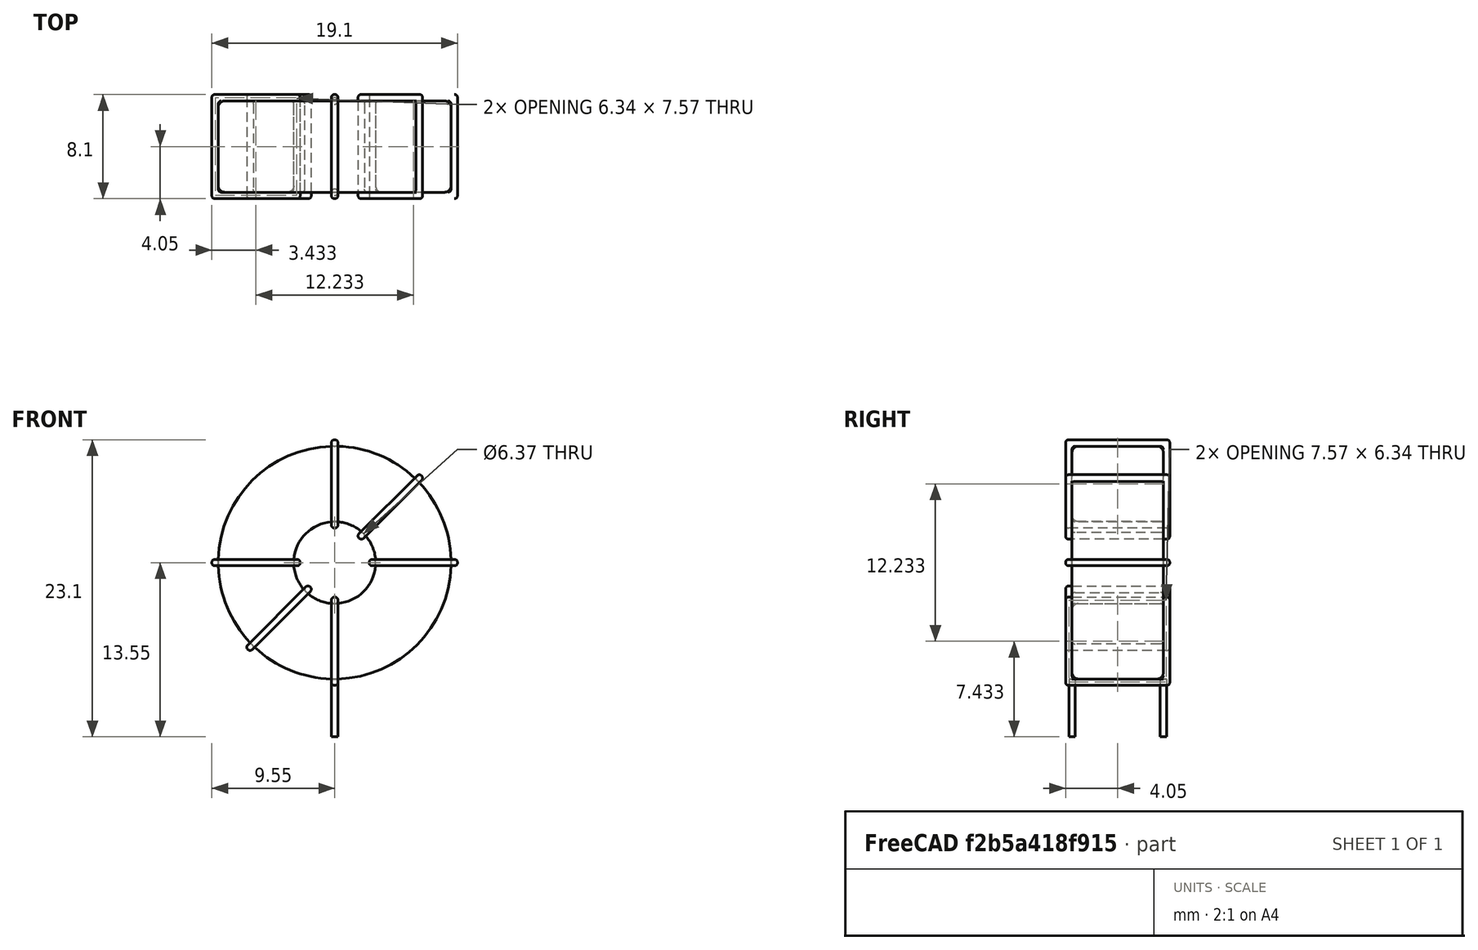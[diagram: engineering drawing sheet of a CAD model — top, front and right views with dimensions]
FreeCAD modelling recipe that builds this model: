
FCSTD DOCUMENT  (FreeCAD 0.16R6703 (Git))
Label: L_Toroid_Vertical_L19.1mm_W8.1mm_P7.10mm_Bourns_5700series
License: All rights reserved
LicenseURL: http://en.wikipedia.org/wiki/All_rights_reserved
objects: Sketcher::SketchObject×6, PartDesign::Pad×6, PartDesign::Fillet×5, Spreadsheet::Sheet×1
note: 23 computed .brp shape members not serialized (recipe doc carries the construction recipe); baked Part::Feature solids carry a one-line shape summary decoded from their .brp

FEATURE [Spreadsheet::Sheet] Spreadsheet  label="dimensions"
  cells = A1=Wx; B1(Wx)=19.1; C1(WW)=6.366666666666667; D1=19.1; A2=Wy; B2(Wy)=8.1; D2=8.1; A3=RM; B3(RMx)=7.1; C3(RMy)=0; A4=d_wire; B4(d_wire)=0.5; A5=H; B5(H)=19.1; A6=offsetx; B6(offsetx)=9.550000000000001
FEATURE [Sketcher::SketchObject] Sketch
  Placement = pos=(0,-3.55,0) rot=(1,0,0;1.5708rad)
  expr: Placement.Base.y = -Spreadsheet.RMx / 2
  expr: Constraints[0] = Spreadsheet.Wx / 2 - Spreadsheet.d_wire
  expr: Constraints[4] = Spreadsheet.WW / 2
  expr: Constraints[2] = Spreadsheet.Wx / 2 + Spreadsheet.d_wire + 0.5
  sketch-geometry (2):
    g0: Circle CenterX=0 CenterY=10.55 CenterZ=0 NormalX=0 NormalY=0 NormalZ=1 Radius=9.05
    g1: Circle CenterX=0 CenterY=10.55 CenterZ=0 NormalX=0 NormalY=0 NormalZ=1 Radius=3.18333
  constraints (5):
    c: Radius(g0) = 9.05
    c: DistanceX(g-1,g0) = 0
    c: DistanceY(g-1,g0) = 10.55
    c: Coincident(g1,g0)
    c: Radius(g1) = 3.18333
FEATURE [PartDesign::Pad] Pad
  Length = 7.1
  Length2 = 100
  Midplane = true
  Placement = pos=(0,-3.55,0) rot=(1,0,0;1.5708rad)
  Sketch = -> Sketch
  Type = 0
  expr: Length = Spreadsheet.Wy - 2 * Spreadsheet.d_wire
FEATURE [Sketcher::SketchObject] Sketch001
  Placement = pos=(0,0,1) rot=(0,0,1;0rad)
  expr: Placement.Base.z = 0.5 + Spreadsheet.d_wire
  expr: Constraints[4] = Spreadsheet.RMy
  expr: Constraints[2] = -Spreadsheet.RMx
  expr: Constraints[1] = Spreadsheet.d_wire / 2
  sketch-geometry (2):
    g0: Circle CenterX=0 CenterY=0 CenterZ=0 NormalX=0 NormalY=0 NormalZ=1 Radius=0.25
    g1: Circle CenterX=0 CenterY=-7.1 CenterZ=0 NormalX=0 NormalY=0 NormalZ=1 Radius=0.25
  constraints (5):
    c: Equal(g0,g1)
    c: Radius(g0) = 0.25
    c: DistanceY(g-1,g1) = -7.1
    c: Coincident(g0,g-1)
    c: DistanceX(g-1,g1) = 0
FEATURE [PartDesign::Pad] Pad001
  Length = 0.5
  Length2 = 4
  Placement = pos=(0,0,1) rot=(0,0,1;0rad)
  Reversed = true
  Sketch = -> Sketch001
  Type = 4
  expr: Length2 = 3.5 + Spreadsheet.d_wire
  expr: Length = Spreadsheet.d_wire
FEATURE [PartDesign::Fillet] Fillet
  Base = -> Pad [Edge6,Edge3,Edge2]
  Placement = pos=(0,-3.55,0) rot=(1,0,0;1.5708rad)
  Radius = 0.5
FEATURE [Sketcher::SketchObject] Sketch003
  Placement = pos=(0,0.5,10.55) rot=(1,0,0;3.14159rad)
  expr: Constraints[18] = Spreadsheet.d_wire
  expr: Constraints[16] = Spreadsheet.d_wire
  expr: Constraints[19] = Spreadsheet.d_wire
  expr: Constraints[17] = Spreadsheet.d_wire
  expr: Placement.Base.y = -1 * (Spreadsheet.RMx - Spreadsheet.Wy) / 2
  expr: Constraints[21] = (Spreadsheet.Wx - Spreadsheet.WW) / 2 - Spreadsheet.d_wire
  expr: Constraints[22] = Spreadsheet.Wx / 2 - Spreadsheet.d_wire
  expr: Constraints[43] = Spreadsheet.d_wire
  expr: Constraints[48] = Spreadsheet.Wx - Spreadsheet.d_wire * 2
  expr: Constraints[49] = Spreadsheet.Wy
  expr: Placement.Base.z = Spreadsheet.Wx / 2 + Spreadsheet.d_wire + 0.5
  sketch-geometry (16):
    g0: LineSegment StartX=-2.68333 StartY=0 StartZ=0 EndX=-9.55 EndY=0 EndZ=0
    g1: LineSegment StartX=-9.55 StartY=0 StartZ=0 EndX=-9.55 EndY=8.1 EndZ=0
    g2: LineSegment StartX=-9.55 StartY=8.1 StartZ=0 EndX=-2.68333 EndY=8.1 EndZ=0
    g3: LineSegment StartX=-2.68333 StartY=8.1 StartZ=0 EndX=-2.68333 EndY=0 EndZ=0
    g4: LineSegment StartX=-9.05 StartY=7.6 StartZ=0 EndX=-3.18333 EndY=7.6 EndZ=0
    g5: LineSegment StartX=-3.18333 StartY=7.6 StartZ=0 EndX=-3.18333 EndY=0.5 EndZ=0
    g6: LineSegment StartX=-3.18333 StartY=0.5 StartZ=0 EndX=-9.05 EndY=0.5 EndZ=0
    g7: LineSegment StartX=-9.05 StartY=0.5 StartZ=0 EndX=-9.05 EndY=7.6 EndZ=0
    g8: LineSegment StartX=2.68333 StartY=8.1 StartZ=0 EndX=9.55 EndY=8.1 EndZ=0
    g9: LineSegment StartX=9.55 StartY=8.1 StartZ=0 EndX=9.55 EndY=0 EndZ=0
    g10: LineSegment StartX=9.55 StartY=0 StartZ=0 EndX=2.68333 EndY=0 EndZ=0
    g11: LineSegment StartX=2.68333 StartY=0 StartZ=0 EndX=2.68333 EndY=8.1 EndZ=0
    g12: LineSegment StartX=3.18333 StartY=7.6 StartZ=0 EndX=9.05 EndY=7.6 EndZ=0
    g13: LineSegment StartX=9.05 StartY=7.6 StartZ=0 EndX=9.05 EndY=0.5 EndZ=0
    g14: LineSegment StartX=9.05 StartY=0.5 StartZ=0 EndX=3.18333 EndY=0.5 EndZ=0
    g15: LineSegment StartX=3.18333 StartY=0.5 StartZ=0 EndX=3.18333 EndY=7.6 EndZ=0
  constraints (50):
    c: Horizontal(g0)
    c: Coincident(g1,g0)
    c: Vertical(g1)
    c: Coincident(g2,g1)
    c: Horizontal(g2)
    c: Coincident(g3,g2)
    c: Coincident(g3,g0)
    c: Vertical(g3)
    c: Coincident(g4,g5)
    c: Coincident(g5,g6)
    c: Coincident(g6,g7)
    c: Coincident(g7,g4)
    c: Horizontal(g4)
    c: Horizontal(g6)
    c: Vertical(g5)
    c: Vertical(g7)
    c: DistanceX(g1,g4) = 0.5
    c: DistanceY(g4,g1) = 0.5
    c: DistanceX(g5,g0) = 0.5
    c: DistanceY(g0,g5) = 0.5
    c: DistanceY(g-1,g0) = 0
    c: DistanceX(g6,g6) = 5.86667
    c: DistanceX(g6,g-1) = 9.05
    c: Coincident(g8,g9)
    c: Coincident(g9,g10)
    c: Coincident(g10,g11)
    c: Coincident(g11,g8)
    c: Horizontal(g8)
    c: Horizontal(g10)
    c: Vertical(g9)
    c: Vertical(g11)
    c: Coincident(g12,g13)
    c: Coincident(g13,g14)
    c: Coincident(g14,g15)
    c: Coincident(g15,g12)
    c: Horizontal(g12)
    c: Horizontal(g14)
    c: Vertical(g13)
    c: Vertical(g15)
    c: DistanceY(g8,g2) = 0
    c: DistanceY(g10,g0) = 0
    c: DistanceY(g14,g5) = 0
    c: DistanceY(g12,g4) = 0
    c: DistanceX(g8,g12) = 0.5
    c: Equal(g8,g2)
    c: Equal(g12,g4)
    c: Equal(g9,g1)
    c: Equal(g13,g7)
    c: DistanceX(g4,g12) = 18.1
    c: DistanceY(g0,g1) = 8.1
FEATURE [PartDesign::Pad] Pad002
  Length = 0.5
  Length2 = 100
  Midplane = true
  Placement = pos=(0,0.5,10.55) rot=(1,0,0;3.14159rad)
  Sketch = -> Sketch003
  Type = 0
  expr: Length = Spreadsheet.d_wire
FEATURE [PartDesign::Fillet] Fillet001
  Base = -> Pad002 [Edge38,Edge41,Edge42,Edge43,Edge29,Edge32,Edge33,Edge34,Edge25,Edge35,Edge36,Edge13,Edge14,Edge15,Edge16,Edge17,Edge18,Edge19,Edge1,Edge2,Edge3,Edge4,Edge5,Edge6,Edge7,Edge37,Edge39,Edge40,Edge20,Edge23,Edge24,Edge21,Edge22,Edge8,Edge9,Edge10,Edge11,Edge12,Edge26,Edge27,+8 more]
  Placement = pos=(0,0.5,10.55) rot=(1,0,0;3.14159rad)
  Radius = 0.235
  expr: Radius = Spreadsheet.d_wire * 0.47
FEATURE [Sketcher::SketchObject] Sketch004
  Placement = pos=(0,0.5,10.55) rot=(0.92388,0,0.382683;3.14159rad)
  expr: Constraints[18] = Spreadsheet.d_wire
  expr: Constraints[16] = Spreadsheet.d_wire
  expr: Constraints[19] = Spreadsheet.d_wire
  expr: Constraints[17] = Spreadsheet.d_wire
  expr: Placement.Base.y = -1 * (Spreadsheet.RMx - Spreadsheet.Wy) / 2
  expr: Constraints[21] = (Spreadsheet.Wx - Spreadsheet.WW) / 2 - Spreadsheet.d_wire
  expr: Constraints[22] = Spreadsheet.Wx / 2 - Spreadsheet.d_wire
  expr: Constraints[43] = Spreadsheet.d_wire
  expr: Constraints[48] = Spreadsheet.Wx - 2 * Spreadsheet.d_wire
  expr: Constraints[49] = Spreadsheet.Wy
  expr: Placement.Base.z = Spreadsheet.Wx / 2 + Spreadsheet.d_wire + 0.5
  sketch-geometry (16):
    g0: LineSegment StartX=-2.68333 StartY=0 StartZ=0 EndX=-9.55 EndY=0 EndZ=0
    g1: LineSegment StartX=-9.55 StartY=0 StartZ=0 EndX=-9.55 EndY=8.1 EndZ=0
    g2: LineSegment StartX=-9.55 StartY=8.1 StartZ=0 EndX=-2.68333 EndY=8.1 EndZ=0
    g3: LineSegment StartX=-2.68333 StartY=8.1 StartZ=0 EndX=-2.68333 EndY=0 EndZ=0
    g4: LineSegment StartX=-9.05 StartY=7.6 StartZ=0 EndX=-3.18333 EndY=7.6 EndZ=0
    g5: LineSegment StartX=-3.18333 StartY=7.6 StartZ=0 EndX=-3.18333 EndY=0.5 EndZ=0
    g6: LineSegment StartX=-3.18333 StartY=0.5 StartZ=0 EndX=-9.05 EndY=0.5 EndZ=0
    g7: LineSegment StartX=-9.05 StartY=0.5 StartZ=0 EndX=-9.05 EndY=7.6 EndZ=0
    g8: LineSegment StartX=2.68333 StartY=8.1 StartZ=0 EndX=9.55 EndY=8.1 EndZ=0
    g9: LineSegment StartX=9.55 StartY=8.1 StartZ=0 EndX=9.55 EndY=0 EndZ=0
    g10: LineSegment StartX=9.55 StartY=0 StartZ=0 EndX=2.68333 EndY=0 EndZ=0
    g11: LineSegment StartX=2.68333 StartY=0 StartZ=0 EndX=2.68333 EndY=8.1 EndZ=0
    g12: LineSegment StartX=3.18333 StartY=7.6 StartZ=0 EndX=9.05 EndY=7.6 EndZ=0
    g13: LineSegment StartX=9.05 StartY=7.6 StartZ=0 EndX=9.05 EndY=0.5 EndZ=0
    g14: LineSegment StartX=9.05 StartY=0.5 StartZ=0 EndX=3.18333 EndY=0.5 EndZ=0
    g15: LineSegment StartX=3.18333 StartY=0.5 StartZ=0 EndX=3.18333 EndY=7.6 EndZ=0
  constraints (50):
    c: Horizontal(g0)
    c: Coincident(g1,g0)
    c: Vertical(g1)
    c: Coincident(g2,g1)
    c: Horizontal(g2)
    c: Coincident(g3,g2)
    c: Coincident(g3,g0)
    c: Vertical(g3)
    c: Coincident(g4,g5)
    c: Coincident(g5,g6)
    c: Coincident(g6,g7)
    c: Coincident(g7,g4)
    c: Horizontal(g4)
    c: Horizontal(g6)
    c: Vertical(g5)
    c: Vertical(g7)
    c: DistanceX(g1,g4) = 0.5
    c: DistanceY(g4,g1) = 0.5
    c: DistanceX(g5,g0) = 0.5
    c: DistanceY(g0,g5) = 0.5
    c: DistanceY(g-1,g0) = 0
    c: DistanceX(g6,g6) = 5.86667
    c: DistanceX(g6,g-1) = 9.05
    c: Coincident(g8,g9)
    c: Coincident(g9,g10)
    c: Coincident(g10,g11)
    c: Coincident(g11,g8)
    c: Horizontal(g8)
    c: Horizontal(g10)
    c: Vertical(g9)
    c: Vertical(g11)
    c: Coincident(g12,g13)
    c: Coincident(g13,g14)
    c: Coincident(g14,g15)
    c: Coincident(g15,g12)
    c: Horizontal(g12)
    c: Horizontal(g14)
    c: Vertical(g13)
    c: Vertical(g15)
    c: DistanceY(g8,g2) = 0
    c: DistanceY(g10,g0) = 0
    c: DistanceY(g14,g5) = 0
    c: DistanceY(g12,g4) = 0
    c: DistanceX(g8,g12) = 0.5
    c: Equal(g8,g2)
    c: Equal(g12,g4)
    c: Equal(g9,g1)
    c: Equal(g13,g7)
    c: DistanceX(g4,g12) = 18.1
    c: DistanceY(g0,g1) = 8.1
FEATURE [PartDesign::Pad] Pad003
  Length = 0.5
  Length2 = 100
  Midplane = true
  Placement = pos=(0,0.5,10.55) rot=(0.92388,0,0.382683;3.14159rad)
  Sketch = -> Sketch004
  Type = 0
  expr: Length = Spreadsheet.d_wire
FEATURE [PartDesign::Fillet] Fillet002
  Base = -> Pad003 [Edge38,Edge41,Edge42,Edge43,Edge29,Edge32,Edge33,Edge34,Edge25,Edge35,Edge36,Edge13,Edge14,Edge15,Edge16,Edge17,Edge18,Edge19,Edge1,Edge2,Edge3,Edge4,Edge5,Edge6,Edge7,Edge37,Edge39,Edge40,Edge20,Edge23,Edge24,Edge21,Edge22,Edge8,Edge9,Edge10,Edge11,Edge12,Edge26,Edge27,+8 more]
  Placement = pos=(0,0.5,10.55) rot=(0.92388,0,0.382683;3.14159rad)
  Radius = 0.235
  expr: Radius = Spreadsheet.d_wire * 0.47
FEATURE [Sketcher::SketchObject] Sketch005
  Placement = pos=(0,0.5,10.55) rot=(0.92388,0,-0.382683;3.14159rad)
  expr: Constraints[18] = Spreadsheet.d_wire
  expr: Constraints[16] = Spreadsheet.d_wire
  expr: Constraints[19] = Spreadsheet.d_wire
  expr: Constraints[17] = Spreadsheet.d_wire
  expr: Placement.Base.y = -1 * (Spreadsheet.RMx - Spreadsheet.Wy) / 2
  expr: Constraints[21] = (Spreadsheet.Wx - Spreadsheet.WW) / 2 - Spreadsheet.d_wire
  expr: Constraints[22] = Spreadsheet.Wx / 2 - Spreadsheet.d_wire
  expr: Constraints[43] = Spreadsheet.d_wire
  expr: Constraints[48] = Spreadsheet.Wx - 2 * Spreadsheet.d_wire
  expr: Constraints[49] = Spreadsheet.Wy
  expr: Placement.Base.z = Spreadsheet.Wx / 2 + Spreadsheet.d_wire + 0.5
  sketch-geometry (16):
    g0: LineSegment StartX=-2.68333 StartY=0 StartZ=0 EndX=-9.55 EndY=0 EndZ=0
    g1: LineSegment StartX=-9.55 StartY=0 StartZ=0 EndX=-9.55 EndY=8.1 EndZ=0
    g2: LineSegment StartX=-9.55 StartY=8.1 StartZ=0 EndX=-2.68333 EndY=8.1 EndZ=0
    g3: LineSegment StartX=-2.68333 StartY=8.1 StartZ=0 EndX=-2.68333 EndY=0 EndZ=0
    g4: LineSegment StartX=-9.05 StartY=7.6 StartZ=0 EndX=-3.18333 EndY=7.6 EndZ=0
    g5: LineSegment StartX=-3.18333 StartY=7.6 StartZ=0 EndX=-3.18333 EndY=0.5 EndZ=0
    g6: LineSegment StartX=-3.18333 StartY=0.5 StartZ=0 EndX=-9.05 EndY=0.5 EndZ=0
    g7: LineSegment StartX=-9.05 StartY=0.5 StartZ=0 EndX=-9.05 EndY=7.6 EndZ=0
    g8: LineSegment StartX=2.68333 StartY=8.1 StartZ=0 EndX=9.55 EndY=8.1 EndZ=0
    g9: LineSegment StartX=9.55 StartY=8.1 StartZ=0 EndX=9.55 EndY=0 EndZ=0
    g10: LineSegment StartX=9.55 StartY=0 StartZ=0 EndX=2.68333 EndY=0 EndZ=0
    g11: LineSegment StartX=2.68333 StartY=0 StartZ=0 EndX=2.68333 EndY=8.1 EndZ=0
    g12: LineSegment StartX=3.18333 StartY=7.6 StartZ=0 EndX=9.05 EndY=7.6 EndZ=0
    g13: LineSegment StartX=9.05 StartY=7.6 StartZ=0 EndX=9.05 EndY=0.5 EndZ=0
    g14: LineSegment StartX=9.05 StartY=0.5 StartZ=0 EndX=3.18333 EndY=0.5 EndZ=0
    g15: LineSegment StartX=3.18333 StartY=0.5 StartZ=0 EndX=3.18333 EndY=7.6 EndZ=0
  constraints (50):
    c: Horizontal(g0)
    c: Coincident(g1,g0)
    c: Vertical(g1)
    c: Coincident(g2,g1)
    c: Horizontal(g2)
    c: Coincident(g3,g2)
    c: Coincident(g3,g0)
    c: Vertical(g3)
    c: Coincident(g4,g5)
    c: Coincident(g5,g6)
    c: Coincident(g6,g7)
    c: Coincident(g7,g4)
    c: Horizontal(g4)
    c: Horizontal(g6)
    c: Vertical(g5)
    c: Vertical(g7)
    c: DistanceX(g1,g4) = 0.5
    c: DistanceY(g4,g1) = 0.5
    c: DistanceX(g5,g0) = 0.5
    c: DistanceY(g0,g5) = 0.5
    c: DistanceY(g-1,g0) = 0
    c: DistanceX(g6,g6) = 5.86667
    c: DistanceX(g6,g-1) = 9.05
    c: Coincident(g8,g9)
    c: Coincident(g9,g10)
    c: Coincident(g10,g11)
    c: Coincident(g11,g8)
    c: Horizontal(g8)
    c: Horizontal(g10)
    c: Vertical(g9)
    c: Vertical(g11)
    c: Coincident(g12,g13)
    c: Coincident(g13,g14)
    c: Coincident(g14,g15)
    c: Coincident(g15,g12)
    c: Horizontal(g12)
    c: Horizontal(g14)
    c: Vertical(g13)
    c: Vertical(g15)
    c: DistanceY(g8,g2) = 0
    c: DistanceY(g10,g0) = 0
    c: DistanceY(g14,g5) = 0
    c: DistanceY(g12,g4) = 0
    c: DistanceX(g8,g12) = 0.5
    c: Equal(g8,g2)
    c: Equal(g12,g4)
    c: Equal(g9,g1)
    c: Equal(g13,g7)
    c: DistanceX(g4,g12) = 18.1
    c: DistanceY(g0,g1) = 8.1
FEATURE [PartDesign::Pad] Pad004
  Length = 0.5
  Length2 = 100
  Midplane = true
  Placement = pos=(0,0.5,10.55) rot=(0.92388,0,-0.382683;3.14159rad)
  Sketch = -> Sketch005
  Type = 0
  expr: Length = Spreadsheet.d_wire
FEATURE [PartDesign::Fillet] Fillet003
  Base = -> Pad004 [Edge38,Edge41,Edge42,Edge43,Edge29,Edge32,Edge33,Edge34,Edge25,Edge35,Edge36,Edge13,Edge14,Edge15,Edge16,Edge17,Edge18,Edge19,Edge1,Edge2,Edge3,Edge4,Edge5,Edge6,Edge7,Edge37,Edge39,Edge40,Edge20,Edge23,Edge24,Edge21,Edge22,Edge8,Edge9,Edge10,Edge11,Edge12,Edge26,Edge27,+8 more]
  Placement = pos=(0,0.5,10.55) rot=(0.92388,0,-0.382683;3.14159rad)
  Radius = 0.235
  expr: Radius = Spreadsheet.d_wire * 0.47
FEATURE [Sketcher::SketchObject] Sketch006
  Placement = pos=(0,0.5,10.55) rot=(0.707107,0,0.707107;3.14159rad)
  expr: Constraints[18] = Spreadsheet.d_wire
  expr: Constraints[16] = Spreadsheet.d_wire
  expr: Constraints[19] = Spreadsheet.d_wire
  expr: Constraints[17] = Spreadsheet.d_wire
  expr: Placement.Base.y = -1 * (Spreadsheet.RMx - Spreadsheet.Wy) / 2
  expr: Constraints[21] = (Spreadsheet.Wx - Spreadsheet.WW) / 2 - Spreadsheet.d_wire
  expr: Constraints[22] = Spreadsheet.Wx / 2 - Spreadsheet.d_wire
  expr: Constraints[43] = Spreadsheet.d_wire
  expr: Constraints[48] = Spreadsheet.Wx - Spreadsheet.d_wire * 2
  expr: Constraints[49] = Spreadsheet.Wy
  expr: Placement.Base.z = Spreadsheet.Wx / 2 + Spreadsheet.d_wire + 0.5
  sketch-geometry (16):
    g0: LineSegment StartX=-2.68333 StartY=0 StartZ=0 EndX=-9.55 EndY=0 EndZ=0
    g1: LineSegment StartX=-9.55 StartY=0 StartZ=0 EndX=-9.55 EndY=8.1 EndZ=0
    g2: LineSegment StartX=-9.55 StartY=8.1 StartZ=0 EndX=-2.68333 EndY=8.1 EndZ=0
    g3: LineSegment StartX=-2.68333 StartY=8.1 StartZ=0 EndX=-2.68333 EndY=0 EndZ=0
    g4: LineSegment StartX=-9.05 StartY=7.6 StartZ=0 EndX=-3.18333 EndY=7.6 EndZ=0
    g5: LineSegment StartX=-3.18333 StartY=7.6 StartZ=0 EndX=-3.18333 EndY=0.5 EndZ=0
    g6: LineSegment StartX=-3.18333 StartY=0.5 StartZ=0 EndX=-9.05 EndY=0.5 EndZ=0
    g7: LineSegment StartX=-9.05 StartY=0.5 StartZ=0 EndX=-9.05 EndY=7.6 EndZ=0
    g8: LineSegment StartX=2.68333 StartY=8.1 StartZ=0 EndX=9.55 EndY=8.1 EndZ=0
    g9: LineSegment StartX=9.55 StartY=8.1 StartZ=0 EndX=9.55 EndY=0 EndZ=0
    g10: LineSegment StartX=9.55 StartY=0 StartZ=0 EndX=2.68333 EndY=0 EndZ=0
    g11: LineSegment StartX=2.68333 StartY=0 StartZ=0 EndX=2.68333 EndY=8.1 EndZ=0
    g12: LineSegment StartX=3.18333 StartY=7.6 StartZ=0 EndX=9.05 EndY=7.6 EndZ=0
    g13: LineSegment StartX=9.05 StartY=7.6 StartZ=0 EndX=9.05 EndY=0.5 EndZ=0
    g14: LineSegment StartX=9.05 StartY=0.5 StartZ=0 EndX=3.18333 EndY=0.5 EndZ=0
    g15: LineSegment StartX=3.18333 StartY=0.5 StartZ=0 EndX=3.18333 EndY=7.6 EndZ=0
  constraints (50):
    c: Horizontal(g0)
    c: Coincident(g1,g0)
    c: Vertical(g1)
    c: Coincident(g2,g1)
    c: Horizontal(g2)
    c: Coincident(g3,g2)
    c: Coincident(g3,g0)
    c: Vertical(g3)
    c: Coincident(g4,g5)
    c: Coincident(g5,g6)
    c: Coincident(g6,g7)
    c: Coincident(g7,g4)
    c: Horizontal(g4)
    c: Horizontal(g6)
    c: Vertical(g5)
    c: Vertical(g7)
    c: DistanceX(g1,g4) = 0.5
    c: DistanceY(g4,g1) = 0.5
    c: DistanceX(g5,g0) = 0.5
    c: DistanceY(g0,g5) = 0.5
    c: DistanceY(g-1,g0) = 0
    c: DistanceX(g6,g6) = 5.86667
    c: DistanceX(g6,g-1) = 9.05
    c: Coincident(g8,g9)
    c: Coincident(g9,g10)
    c: Coincident(g10,g11)
    c: Coincident(g11,g8)
    c: Horizontal(g8)
    c: Horizontal(g10)
    c: Vertical(g9)
    c: Vertical(g11)
    c: Coincident(g12,g13)
    c: Coincident(g13,g14)
    c: Coincident(g14,g15)
    c: Coincident(g15,g12)
    c: Horizontal(g12)
    c: Horizontal(g14)
    c: Vertical(g13)
    c: Vertical(g15)
    c: DistanceY(g8,g2) = 0
    c: DistanceY(g10,g0) = 0
    c: DistanceY(g14,g5) = 0
    c: DistanceY(g12,g4) = 0
    c: DistanceX(g8,g12) = 0.5
    c: Equal(g8,g2)
    c: Equal(g12,g4)
    c: Equal(g9,g1)
    c: Equal(g13,g7)
    c: DistanceX(g4,g12) = 18.1
    c: DistanceY(g0,g1) = 8.1
FEATURE [PartDesign::Pad] Pad005
  Length = 0.5
  Length2 = 100
  Midplane = true
  Placement = pos=(0,0.5,10.55) rot=(0.707107,0,0.707107;3.14159rad)
  Sketch = -> Sketch006
  Type = 0
  expr: Length = Spreadsheet.d_wire
FEATURE [PartDesign::Fillet] Fillet004
  Base = -> Pad005 [Edge38,Edge41,Edge42,Edge43,Edge29,Edge32,Edge33,Edge34,Edge25,Edge35,Edge36,Edge13,Edge14,Edge15,Edge16,Edge17,Edge18,Edge19,Edge1,Edge2,Edge3,Edge4,Edge5,Edge6,Edge7,Edge37,Edge39,Edge40,Edge20,Edge23,Edge24,Edge21,Edge22,Edge8,Edge9,Edge10,Edge11,Edge12,Edge26,Edge27,+8 more]
  Placement = pos=(0,0.5,10.55) rot=(0.707107,0,0.707107;3.14159rad)
  Radius = 0.235
  expr: Radius = Spreadsheet.d_wire * 0.47
